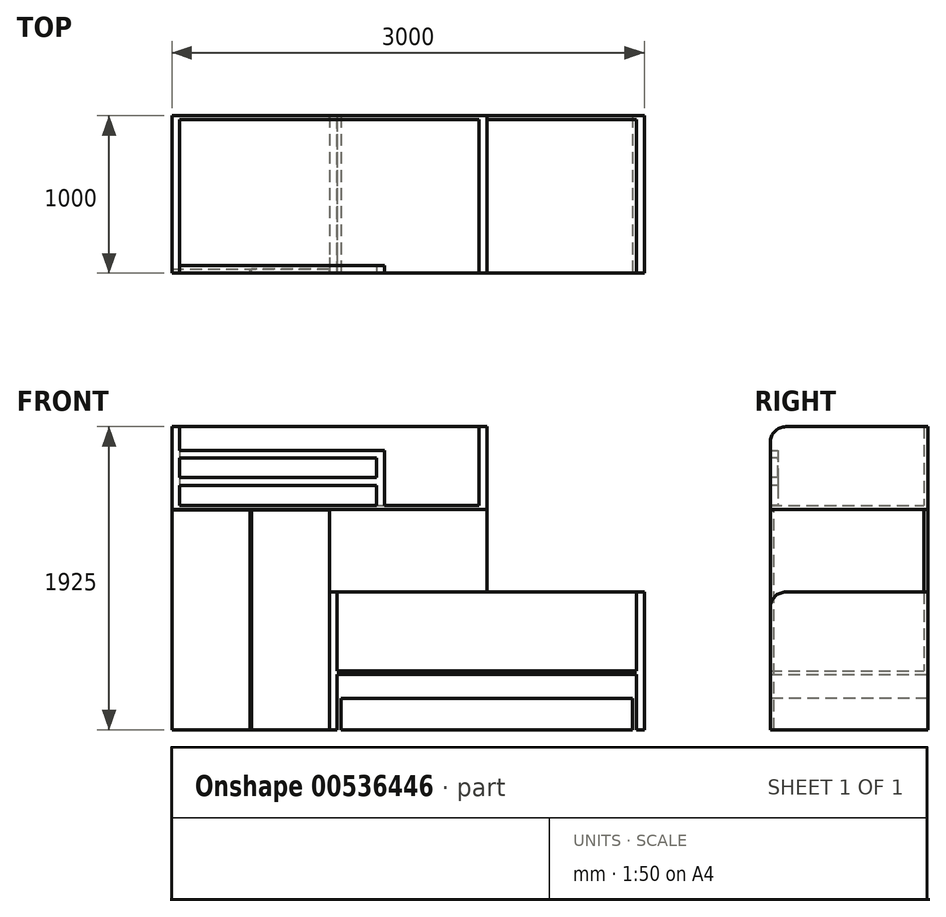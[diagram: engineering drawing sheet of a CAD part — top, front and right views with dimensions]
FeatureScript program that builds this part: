
annotation { "Feature Type Name" : "Feature", "Feature Type Description" : "" }
export const myFeature = defineFeature(function(context is Context, id is Id, definition is map)
    precondition{}
    {
        {
            var Q0;
            Q0=qCreatedBy(makeId("Top.planeOp"),FACE);
            var sketch = newSketch(context, id + "F0", { "sketchPlane" : qUnion([Q0])});
            skLineSegment(sketch, "E0.bottom", {"start": v(0, 0) * mm, "end": v(-2000, 0) * mm});
            skLineSegment(sketch, "E0.top", {"start": v(0, 1000) * mm, "end": v(-2000, 1000) * mm});
            skLineSegment(sketch, "E0.left", {"start": v(0, 0) * mm, "end": v(0, 1000) * mm});
            skLineSegment(sketch, "E0.right", {"start": v(-2000, 0) * mm, "end": v(-2000, 1000) * mm});
            skSolve(sketch);
        }
        {
            var Q0;
            Q0=makeQuery(id+"F0.imprint","IMPRINT",FACE,{"disambiguationData":[TD([[makeQuery(id+"F0.imprint","IMPRINT",EDGE,{"derivedFrom":sQuery(id+"F0.wireOp",EDGE,"E0.bottom")}),-1.0]])]});
            extrude(context, id + "F1", {"entities" : qUnion([Q0]), "depth" : 25 * mm, "offsetDistance" : 25 * mm});
        }
        {
            var Q0;
            Q0=makeQuery(id+"F1.opExtrude","CAP_FACE",FACE,{"disambiguationData":[OSD([sQuery(id+"F0.wireOp",EDGE,"E0.bottom"),sQuery(id+"F0.wireOp",EDGE,"E0.top"),sQuery(id+"F0.wireOp",EDGE,"E0.left"),sQuery(id+"F0.wireOp",EDGE,"E0.right")])],"isStart":false});
            var sketch = newSketch(context, id + "F2", { "sketchPlane" : qUnion([Q0])});
            skLineSegment(sketch, "E1.bottom", {"start": v(0, 0) * mm, "end": v(-50, 0) * mm});
            skLineSegment(sketch, "E1.top", {"start": v(0, 1000) * mm, "end": v(-50, 1000) * mm});
            skLineSegment(sketch, "E1.left", {"start": v(0, 0) * mm, "end": v(0, 1000) * mm});
            skLineSegment(sketch, "E1.right", {"start": v(-50, 0) * mm, "end": v(-50, 1000) * mm});
            skSolve(sketch);
        }
        {
            var Q0;
            Q0=makeQuery(id+"F2.imprint","IMPRINT",FACE,{"disambiguationData":[TD([[makeQuery(id+"F2.imprint","IMPRINT",EDGE,{"derivedFrom":sQuery(id+"F2.wireOp",EDGE,"E1.bottom")}),-1.0]])]});
            extrude(context, id + "F3", {"entities" : qUnion([Q0]), "operationType" : NewBodyOperationType.ADD, "depth" : 500 * mm, "offsetDistance" : 25 * mm});
        }
        {
            var Q0;
            Q0=makeQuery(id+"F1.opExtrude","CAP_FACE",FACE,{"disambiguationData":[OSD([sQuery(id+"F0.wireOp",EDGE,"E0.bottom"),sQuery(id+"F0.wireOp",EDGE,"E0.top"),sQuery(id+"F0.wireOp",EDGE,"E0.left"),sQuery(id+"F0.wireOp",EDGE,"E0.right")])],"isStart":false});
            var sketch = newSketch(context, id + "F4", { "sketchPlane" : qUnion([Q0])});
            skLineSegment(sketch, "E2.bottom", {"start": v(-2000, 0) * mm, "end": v(-1950, 0) * mm});
            skLineSegment(sketch, "E2.top", {"start": v(-2000, 1000) * mm, "end": v(-1950, 1000) * mm});
            skLineSegment(sketch, "E2.left", {"start": v(-2000, 0) * mm, "end": v(-2000, 1000) * mm});
            skLineSegment(sketch, "E2.right", {"start": v(-1950, 0) * mm, "end": v(-1950, 1000) * mm});
            skSolve(sketch);
        }
        {
            var Q0;
            Q0=makeQuery(id+"F4.imprint","IMPRINT",FACE,{"disambiguationData":[TD([[makeQuery(id+"F4.imprint","IMPRINT",EDGE,{"derivedFrom":sQuery(id+"F4.wireOp",EDGE,"E2.bottom")}),-1.0]])]});
            extrude(context, id + "F5", {"entities" : qUnion([Q0]), "operationType" : NewBodyOperationType.ADD, "depth" : 500 * mm, "offsetDistance" : 25 * mm});
        }
        {
            var Q0;
            Q0=makeQuery(id+"F5.opExtrude","CAP_EDGE",EDGE,{"disambiguationData":[OSD([sQuery(id+"F4.wireOp",EDGE,"E2.bottom")])],"isStart":false});
            var Q1;
            Q1=makeQuery(id+"F3.opExtrude","CAP_EDGE",EDGE,{"disambiguationData":[OSD([sQuery(id+"F2.wireOp",EDGE,"E1.bottom")])],"isStart":false});
            fillet(context, id + "F6", {"entities" : qUnion([Q0, Q1]), "radius" : 100 * mm, "tangentPropagation" : true, "allowEdgeOverflow" : false});
        }
        {
            var Q0;
            Q0=makeQuery(id+"F1.opExtrude","CAP_FACE",FACE,{"disambiguationData":[OSD([sQuery(id+"F0.wireOp",EDGE,"E0.bottom"),sQuery(id+"F0.wireOp",EDGE,"E0.top"),sQuery(id+"F0.wireOp",EDGE,"E0.left"),sQuery(id+"F0.wireOp",EDGE,"E0.right")])],"isStart":false});
            var sketch = newSketch(context, id + "F7", { "sketchPlane" : qUnion([Q0])});
            skLineSegment(sketch, "E3.bottom", {"start": v(-1950, 0) * mm, "end": v(-650, 0) * mm});
            skLineSegment(sketch, "E3.top", {"start": v(-1950, 50) * mm, "end": v(-650, 50) * mm});
            skLineSegment(sketch, "E3.left", {"start": v(-1950, 0) * mm, "end": v(-1950, 50) * mm});
            skLineSegment(sketch, "E3.right", {"start": v(-650, 0) * mm, "end": v(-650, 50) * mm});
            skSolve(sketch);
        }
        {
            var Q0;
            Q0=makeQuery(id+"F7.imprint","IMPRINT",FACE,{"disambiguationData":[TD([[makeQuery(id+"F7.imprint","IMPRINT",EDGE,{"derivedFrom":sQuery(id+"F7.wireOp",EDGE,"E3.bottom")}),-1.0]])]});
            extrude(context, id + "F8", {"entities" : qUnion([Q0]), "operationType" : NewBodyOperationType.ADD, "depth" : 350 * mm, "offsetDistance" : 25 * mm});
        }
        {
            var Q0;
            Q0=makeQuery(id+"F8.boolean.opBoolean","MERGE",FACE,{"derivedFrom":[makeQuery(id+"F5.boolean.opBoolean","MERGE",FACE,{"derivedFrom":[makeQuery(id+"F3.boolean.opBoolean","MERGE",FACE,{"derivedFrom":[makeQuery(id+"F1.opExtrude","SWEPT_FACE",FACE,{"disambiguationData":[OSD([sQuery(id+"F0.wireOp",EDGE,"E0.bottom")])]}),makeQuery(id+"F3.opExtrude","SWEPT_FACE",FACE,{"disambiguationData":[OSD([sQuery(id+"F2.wireOp",EDGE,"E1.bottom")])]})]}),makeQuery(id+"F5.opExtrude","SWEPT_FACE",FACE,{"disambiguationData":[OSD([sQuery(id+"F4.wireOp",EDGE,"E2.bottom")])]})]}),makeQuery(id+"F8.opExtrude","SWEPT_FACE",FACE,{"disambiguationData":[OSD([sQuery(id+"F7.wireOp",EDGE,"E3.bottom")])]})]});
            var sketch = newSketch(context, id + "F9", { "sketchPlane" : qUnion([Q0])});
            skLineSegment(sketch, "E4.bottom", {"start": v(-700, 325) * mm, "end": v(-1950, 325) * mm});
            skLineSegment(sketch, "E4.top", {"start": v(-700, 202.99) * mm, "end": v(-1950, 202.99) * mm});
            skLineSegment(sketch, "E4.left", {"start": v(-700, 325) * mm, "end": v(-700, 202.99) * mm});
            skLineSegment(sketch, "E4.right", {"start": v(-1950, 325) * mm, "end": v(-1950, 202.99) * mm});
            skLineSegment(sketch, "E5.bottom", {"start": v(-700, 25) * mm, "end": v(-1950, 25) * mm});
            skLineSegment(sketch, "E5.top", {"start": v(-700, 152.99) * mm, "end": v(-1950, 152.99) * mm});
            skLineSegment(sketch, "E5.left", {"start": v(-700, 25) * mm, "end": v(-700, 152.99) * mm});
            skLineSegment(sketch, "E5.right", {"start": v(-1950, 25) * mm, "end": v(-1950, 152.99) * mm});
            skSolve(sketch);
        }
        {
            var Q0;
            Q0=makeQuery(id+"F9.imprint","IMPRINT",FACE,{"disambiguationData":[TD([[makeQuery(id+"F9.imprint","IMPRINT",EDGE,{"derivedFrom":sQuery(id+"F9.wireOp",EDGE,"E4.bottom")}),1.0]])]});
            var Q1;
            Q1=makeQuery(id+"F9.imprint","IMPRINT",FACE,{"disambiguationData":[TD([[makeQuery(id+"F9.imprint","IMPRINT",EDGE,{"derivedFrom":sQuery(id+"F9.wireOp",EDGE,"E5.bottom")}),-1.0]])]});
            extrude(context, id + "F10", {"entities" : qUnion([Q0, Q1]), "operationType" : NewBodyOperationType.REMOVE, "endBound" : BoundingType.THROUGH_ALL, "oppositeDirection" : true, "depth" : 25 * mm, "offsetDistance" : 25 * mm});
        }
        {
            var Q0;
            Q0=makeQuery(id+"F1.opExtrude","CAP_FACE",FACE,{"disambiguationData":[OSD([sQuery(id+"F0.wireOp",EDGE,"E0.bottom"),sQuery(id+"F0.wireOp",EDGE,"E0.top"),sQuery(id+"F0.wireOp",EDGE,"E0.left"),sQuery(id+"F0.wireOp",EDGE,"E0.right")])],"isStart":true});
            var sketch = newSketch(context, id + "F11", { "sketchPlane" : qUnion([Q0])});
            skLineSegment(sketch, "E6.bottom", {"start": v(-2000, -1000) * mm, "end": v(-1000, -1000) * mm});
            skLineSegment(sketch, "E6.top", {"start": v(-2000, -25) * mm, "end": v(-1000, -25) * mm});
            skLineSegment(sketch, "E6.left", {"start": v(-2000, -1000) * mm, "end": v(-2000, -25) * mm});
            skLineSegment(sketch, "E6.right", {"start": v(-1000, -1000) * mm, "end": v(-1000, -25) * mm});
            skSolve(sketch);
        }
        {
            var Q0;
            Q0=makeQuery(id+"F11.imprint","IMPRINT",FACE,{"disambiguationData":[TD([[makeQuery(id+"F11.imprint","IMPRINT",EDGE,{"derivedFrom":sQuery(id+"F11.wireOp",EDGE,"E6.bottom")}),-1.0]])]});
            extrude(context, id + "F12", {"entities" : qUnion([Q0]), "operationType" : NewBodyOperationType.ADD, "depth" : 1400 * mm, "offsetDistance" : 25 * mm});
        }
        {
            var Q0;
            Q0=makeQuery(id+"F12.opExtrude","SWEPT_FACE",FACE,{"disambiguationData":[OSD([sQuery(id+"F11.wireOp",EDGE,"E6.top")])]});
            var sketch = newSketch(context, id + "F13", { "sketchPlane" : qUnion([Q0])});
            skLineSegment(sketch, "E7.bottom", {"start": v(-2000, -1400) * mm, "end": v(-1505, -1400) * mm});
            skLineSegment(sketch, "E7.top", {"start": v(-2000, -5) * mm, "end": v(-1505, -5) * mm});
            skLineSegment(sketch, "E7.left", {"start": v(-2000, -1400) * mm, "end": v(-2000, -5) * mm});
            skLineSegment(sketch, "E7.right", {"start": v(-1505, -1400) * mm, "end": v(-1505, -5) * mm});
            skLineSegment(sketch, "E8.bottom", {"start": v(-1000, -1400) * mm, "end": v(-1495, -1400) * mm});
            skLineSegment(sketch, "E8.top", {"start": v(-1000, -5) * mm, "end": v(-1495, -5) * mm});
            skLineSegment(sketch, "E8.left", {"start": v(-1000, -1400) * mm, "end": v(-1000, -5) * mm});
            skLineSegment(sketch, "E8.right", {"start": v(-1495, -1400) * mm, "end": v(-1495, -5) * mm});
            skSolve(sketch);
        }
        {
            var Q0;
            Q0=makeQuery(id+"F13.imprint","IMPRINT",FACE,{"disambiguationData":[TD([[makeQuery(id+"F13.imprint","IMPRINT",EDGE,{"derivedFrom":sQuery(id+"F13.wireOp",EDGE,"E7.bottom")}),1.0]])]});
            var Q1;
            Q1=makeQuery(id+"F13.imprint","IMPRINT",FACE,{"disambiguationData":[TD([[makeQuery(id+"F13.imprint","IMPRINT",EDGE,{"derivedFrom":sQuery(id+"F13.wireOp",EDGE,"E8.bottom")}),1.0]])]});
            extrude(context, id + "F14", {"entities" : qUnion([Q0, Q1]), "operationType" : NewBodyOperationType.ADD, "depth" : 25 * mm, "offsetDistance" : 25 * mm});
        }
        {
            var Q0;
            Q0=makeQuery(id+"F10.boolean.opBoolean","MERGE",FACE,{"derivedFrom":[makeQuery(id+"F1.opExtrude","CAP_FACE",FACE,{"disambiguationData":[OSD([sQuery(id+"F0.wireOp",EDGE,"E0.bottom"),sQuery(id+"F0.wireOp",EDGE,"E0.top"),sQuery(id+"F0.wireOp",EDGE,"E0.left"),sQuery(id+"F0.wireOp",EDGE,"E0.right")])],"isStart":false}),makeQuery(id+"F10.opExtrude","SWEPT_FACE",FACE,{"disambiguationData":[OSD([sQuery(id+"F9.wireOp",EDGE,"E5.bottom")])]})]});
            var sketch = newSketch(context, id + "F15", { "sketchPlane" : qUnion([Q0])});
            skLineSegment(sketch, "E9.bottom", {"start": v(-1950, 1000) * mm, "end": v(-50, 1000) * mm});
            skLineSegment(sketch, "E9.top", {"start": v(-1950, 975) * mm, "end": v(-50, 975) * mm});
            skLineSegment(sketch, "E9.left", {"start": v(-1950, 1000) * mm, "end": v(-1950, 975) * mm});
            skLineSegment(sketch, "E9.right", {"start": v(-50, 1000) * mm, "end": v(-50, 975) * mm});
            skSolve(sketch);
        }
        {
            var Q0;
            Q0=makeQuery(id+"F15.imprint","IMPRINT",FACE,{"disambiguationData":[TD([[makeQuery(id+"F15.imprint","IMPRINT",EDGE,{"derivedFrom":sQuery(id+"F15.wireOp",EDGE,"E9.bottom")}),1.0]])]});
            extrude(context, id + "F16", {"entities" : qUnion([Q0]), "operationType" : NewBodyOperationType.ADD, "depth" : 500 * mm, "offsetDistance" : 25 * mm});
        }
        {
            var Q0;
            Q0=makeQuery(id+"F14.boolean.opBoolean","MERGE",FACE,{"derivedFrom":[makeQuery(id+"F12.opExtrude","SWEPT_FACE",FACE,{"disambiguationData":[OSD([sQuery(id+"F11.wireOp",EDGE,"E6.right")])]}),makeQuery(id+"F14.opExtrude","SWEPT_FACE",FACE,{"disambiguationData":[OSD([sQuery(id+"F13.wireOp",EDGE,"E8.left")])]})]});
            var sketch = newSketch(context, id + "F17", { "sketchPlane" : qUnion([Q0])});
            skLineSegment(sketch, "E10.bottom", {"start": v(1000, -1400) * mm, "end": v(0, -1400) * mm});
            skLineSegment(sketch, "E10.top", {"start": v(1000, -525) * mm, "end": v(0, -525) * mm});
            skLineSegment(sketch, "E10.left", {"start": v(1000, -1400) * mm, "end": v(1000, -525) * mm});
            skLineSegment(sketch, "E10.right", {"start": v(0, -1400) * mm, "end": v(0, -525) * mm});
            skSolve(sketch);
        }
        {
            var Q0;
            Q0=makeQuery(id+"F17.imprint","IMPRINT",FACE,{"disambiguationData":[TD([[makeQuery(id+"F17.imprint","IMPRINT",EDGE,{"derivedFrom":sQuery(id+"F17.wireOp",EDGE,"E10.bottom")}),-1.0]])]});
            extrude(context, id + "F18", {"entities" : qUnion([Q0]), "depth" : 50 * mm, "offsetDistance" : 25 * mm});
        }
        {
            var Q0;
            Q0=makeQuery(id+"F18.opExtrude","CAP_FACE",FACE,{"disambiguationData":[OSD([sQuery(id+"F17.wireOp",EDGE,"E10.bottom"),sQuery(id+"F17.wireOp",EDGE,"E10.top"),sQuery(id+"F17.wireOp",EDGE,"E10.left"),sQuery(id+"F17.wireOp",EDGE,"E10.right")])],"isStart":false});
            var sketch = newSketch(context, id + "F19", { "sketchPlane" : qUnion([Q0])});
            skLineSegment(sketch, "E11.bottom", {"start": v(0, -1025) * mm, "end": v(1000, -1025) * mm});
            skLineSegment(sketch, "E11.top", {"start": v(0, -1050) * mm, "end": v(1000, -1050) * mm});
            skLineSegment(sketch, "E11.left", {"start": v(0, -1025) * mm, "end": v(0, -1050) * mm});
            skLineSegment(sketch, "E11.right", {"start": v(1000, -1025) * mm, "end": v(1000, -1050) * mm});
            skSolve(sketch);
        }
        {
            var Q0;
            Q0=makeQuery(id+"F19.imprint","IMPRINT",FACE,{"disambiguationData":[TD([[makeQuery(id+"F19.imprint","IMPRINT",EDGE,{"derivedFrom":sQuery(id+"F19.wireOp",EDGE,"E11.bottom")}),-1.0]])]});
            extrude(context, id + "F20", {"entities" : qUnion([Q0]), "operationType" : NewBodyOperationType.ADD, "depth" : (2000 - 50 - 50) * mm, "offsetDistance" : 25 * mm});
        }
        {
            var Q0;
            Q0=makeQuery(id+"F20.opExtrude","CAP_FACE",FACE,{"disambiguationData":[OSD([sQuery(id+"F19.wireOp",EDGE,"E11.bottom"),sQuery(id+"F19.wireOp",EDGE,"E11.top"),sQuery(id+"F19.wireOp",EDGE,"E11.left"),sQuery(id+"F19.wireOp",EDGE,"E11.right")])],"isStart":false});
            var sketch = newSketch(context, id + "F21", { "sketchPlane" : qUnion([Q0])});
            skLineSegment(sketch, "E12.0.0", {"start": v(0, -525) * mm, "end": v(0, -1025) * mm});
            skLineSegment(sketch, "E12.0.1", {"start": v(0, -1025) * mm, "end": v(1000, -1025) * mm});
            skLineSegment(sketch, "E12.0.2", {"start": v(1000, -1025) * mm, "end": v(1000, -525) * mm});
            skLineSegment(sketch, "E12.0.3", {"start": v(1000, -525) * mm, "end": v(0, -525) * mm});
            skLineSegment(sketch, "E13.0.0", {"start": v(1000, -1050) * mm, "end": v(0, -1050) * mm});
            skLineSegment(sketch, "E13.0.1", {"start": v(0, -1050) * mm, "end": v(0, -1400) * mm});
            skLineSegment(sketch, "E13.0.2", {"start": v(0, -1400) * mm, "end": v(1000, -1400) * mm});
            skLineSegment(sketch, "E13.0.3", {"start": v(1000, -1400) * mm, "end": v(1000, -1050) * mm});
            skSolve(sketch);
        }
        {
            var Q0;
            Q0=makeQuery(id+"F21.imprint","IMPRINT",FACE,{"disambiguationData":[TD([[makeQuery(id+"F21.imprint","IMPRINT",EDGE,{"derivedFrom":sQuery(id+"F21.wireOp",EDGE,"E12.0.0")}),1.0]])]});
            var Q1;
            Q1=makeQuery(id+"F21.imprint","IMPRINT",FACE,{"disambiguationData":[TD([[makeQuery(id+"F21.imprint","IMPRINT",EDGE,{"derivedFrom":sQuery(id+"F21.wireOp",EDGE,"E12.0.1")}),-1.0]])]});
            var Q2;
            Q2=makeQuery(id+"F21.imprint","IMPRINT",FACE,{"disambiguationData":[TD([[makeQuery(id+"F21.imprint","IMPRINT",EDGE,{"derivedFrom":sQuery(id+"F21.wireOp",EDGE,"E13.0.0")}),-1.0]])]});
            extrude(context, id + "F22", {"entities" : qUnion([Q0, Q1, Q2]), "operationType" : NewBodyOperationType.ADD, "depth" : 50 * mm, "offsetDistance" : 25 * mm});
        }
        {
            var Q0;
            Q0=makeQuery(id+"F18.opExtrude","SWEPT_EDGE",EDGE,{"disambiguationData":[OSD([sQuery(id+"F13.wireOp",EDGE,"E8.left"),sQuery(id+"F17.wireOp",EDGE,"E10.top"),sQuery(id+"F17.wireOp",EDGE,"E10.right")])]});
            var Q1;
            Q1=makeQuery(id+"F22.opExtrude","SWEPT_EDGE",EDGE,{"disambiguationData":[OSD([sQuery(id+"F21.wireOp",EDGE,"E12.0.0"),sQuery(id+"F21.wireOp",EDGE,"E12.0.3")])]});
            fillet(context, id + "F23", {"entities" : qUnion([Q0, Q1]), "radius" : 100 * mm, "tangentPropagation" : true, "allowEdgeOverflow" : false});
        }
        {
            var Q0;
            Q0=makeQuery(id+"F20.opExtrude","SWEPT_FACE",FACE,{"disambiguationData":[OSD([sQuery(id+"F19.wireOp",EDGE,"E11.bottom")])]});
            var sketch = newSketch(context, id + "F24", { "sketchPlane" : qUnion([Q0])});
            skLineSegment(sketch, "E14.bottom", {"start": v(-950, 1000) * mm, "end": v(950, 1000) * mm});
            skLineSegment(sketch, "E14.top", {"start": v(-950, 975) * mm, "end": v(950, 975) * mm});
            skLineSegment(sketch, "E14.left", {"start": v(-950, 1000) * mm, "end": v(-950, 975) * mm});
            skLineSegment(sketch, "E14.right", {"start": v(950, 1000) * mm, "end": v(950, 975) * mm});
            skSolve(sketch);
        }
        {
            var Q0;
            Q0=makeQuery(id+"F24.imprint","IMPRINT",FACE,{"disambiguationData":[TD([[makeQuery(id+"F24.imprint","IMPRINT",EDGE,{"derivedFrom":sQuery(id+"F24.wireOp",EDGE,"E14.bottom")}),1.0]])]});
            extrude(context, id + "F25", {"entities" : qUnion([Q0]), "operationType" : NewBodyOperationType.ADD, "depth" : 500 * mm, "offsetDistance" : 25 * mm});
        }
        {
            var Q0;
            {var subQ0=sQuery(id+"F19.wireOp",EDGE,"E11.right");Q0=makeQuery(id+"F25.boolean.opBoolean","MERGE",FACE,{"derivedFrom":[makeQuery(id+"F22.boolean.opBoolean","MERGE",FACE,{"derivedFrom":[makeQuery(id+"F20.boolean.opBoolean","MERGE",FACE,{"derivedFrom":[makeQuery(id+"F18.opExtrude","SWEPT_FACE",FACE,{"disambiguationData":[OSD([sQuery(id+"F17.wireOp",EDGE,"E10.left")])]}),makeQuery(id+"F20.opExtrude","SWEPT_FACE",FACE,{"disambiguationData":[OSD([subQ0])]})]}),makeQuery(id+"F22.opExtrude","SWEPT_FACE",FACE,{"disambiguationData":[OSD([subQ0,sQuery(id+"F21.wireOp",EDGE,"E12.0.2"),sQuery(id+"F21.wireOp",EDGE,"E13.0.3")])]})]}),makeQuery(id+"F25.opExtrude","SWEPT_FACE",FACE,{"disambiguationData":[OSD([sQuery(id+"F24.wireOp",EDGE,"E14.bottom")])]})]});}
            var sketch = newSketch(context, id + "F26", { "sketchPlane" : qUnion([Q0])});
            skLineSegment(sketch, "E15.bottom", {"start": v(1000, -525) * mm, "end": v(0, -525) * mm});
            skLineSegment(sketch, "E15.top", {"start": v(1000, 0) * mm, "end": v(0, 0) * mm});
            skLineSegment(sketch, "E15.left", {"start": v(1000, -525) * mm, "end": v(1000, 0) * mm});
            skLineSegment(sketch, "E15.right", {"start": v(0, -525) * mm, "end": v(0, 0) * mm});
            skSolve(sketch);
        }
        {
            var Q0;
            Q0=makeQuery(id+"F26.imprint","IMPRINT",FACE,{"disambiguationData":[TD([[makeQuery(id+"F26.imprint","IMPRINT",EDGE,{"derivedFrom":sQuery(id+"F26.wireOp",EDGE,"E15.bottom")}),1.0]])]});
            extrude(context, id + "F27", {"entities" : qUnion([Q0]), "oppositeDirection" : true, "depth" : 25 * mm, "offsetDistance" : 25 * mm});
        }
        {
            var Q0;
            {var subQ0=sQuery(id+"F19.wireOp",EDGE,"E11.left");Q0=makeQuery(id+"F22.boolean.opBoolean","MERGE",FACE,{"derivedFrom":[makeQuery(id+"F20.boolean.opBoolean","MERGE",FACE,{"derivedFrom":[makeQuery(id+"F18.opExtrude","SWEPT_FACE",FACE,{"disambiguationData":[OSD([sQuery(id+"F17.wireOp",EDGE,"E10.right")])]}),makeQuery(id+"F20.opExtrude","SWEPT_FACE",FACE,{"disambiguationData":[OSD([subQ0])]})]}),makeQuery(id+"F22.opExtrude","SWEPT_FACE",FACE,{"disambiguationData":[OSD([subQ0,sQuery(id+"F21.wireOp",EDGE,"E12.0.0"),sQuery(id+"F21.wireOp",EDGE,"E13.0.1")])]})]});}
            var sketch = newSketch(context, id + "F28", { "sketchPlane" : qUnion([Q0])});
            skLineSegment(sketch, "E16.bottom", {"start": v(-925, -1400) * mm, "end": v(925, -1400) * mm});
            skLineSegment(sketch, "E16.top", {"start": v(-925, -1200) * mm, "end": v(925, -1200) * mm});
            skLineSegment(sketch, "E16.left", {"start": v(-925, -1400) * mm, "end": v(-925, -1200) * mm});
            skLineSegment(sketch, "E16.right", {"start": v(925, -1400) * mm, "end": v(925, -1200) * mm});
            skSolve(sketch);
        }
        {
            var Q0;
            Q0=makeQuery(id+"F28.imprint","IMPRINT",FACE,{"disambiguationData":[TD([[makeQuery(id+"F28.imprint","IMPRINT",EDGE,{"derivedFrom":sQuery(id+"F28.wireOp",EDGE,"E16.bottom")}),1.0]])]});
            var Q1;
            {var subQ0=sQuery(id+"F19.wireOp",EDGE,"E11.right");Q1=makeQuery(id+"F25.boolean.opBoolean","MERGE",FACE,{"derivedFrom":[makeQuery(id+"F22.boolean.opBoolean","MERGE",FACE,{"derivedFrom":[makeQuery(id+"F20.boolean.opBoolean","MERGE",FACE,{"derivedFrom":[makeQuery(id+"F18.opExtrude","SWEPT_FACE",FACE,{"disambiguationData":[OSD([sQuery(id+"F17.wireOp",EDGE,"E10.left")])]}),makeQuery(id+"F20.opExtrude","SWEPT_FACE",FACE,{"disambiguationData":[OSD([subQ0])]})]}),makeQuery(id+"F22.opExtrude","SWEPT_FACE",FACE,{"disambiguationData":[OSD([subQ0,sQuery(id+"F21.wireOp",EDGE,"E12.0.2"),sQuery(id+"F21.wireOp",EDGE,"E13.0.3")])]})]}),makeQuery(id+"F25.opExtrude","SWEPT_FACE",FACE,{"disambiguationData":[OSD([sQuery(id+"F24.wireOp",EDGE,"E14.bottom")])]})]});}
            extrude(context, id + "F29", {"entities" : qUnion([Q0]), "endBound" : BoundingType.UP_TO_SURFACE, "oppositeDirection" : true, "depth" : 914 * mm, "endBoundEntityFace" : qUnion([Q1]), "offsetDistance" : 25 * mm});
        }
    });
